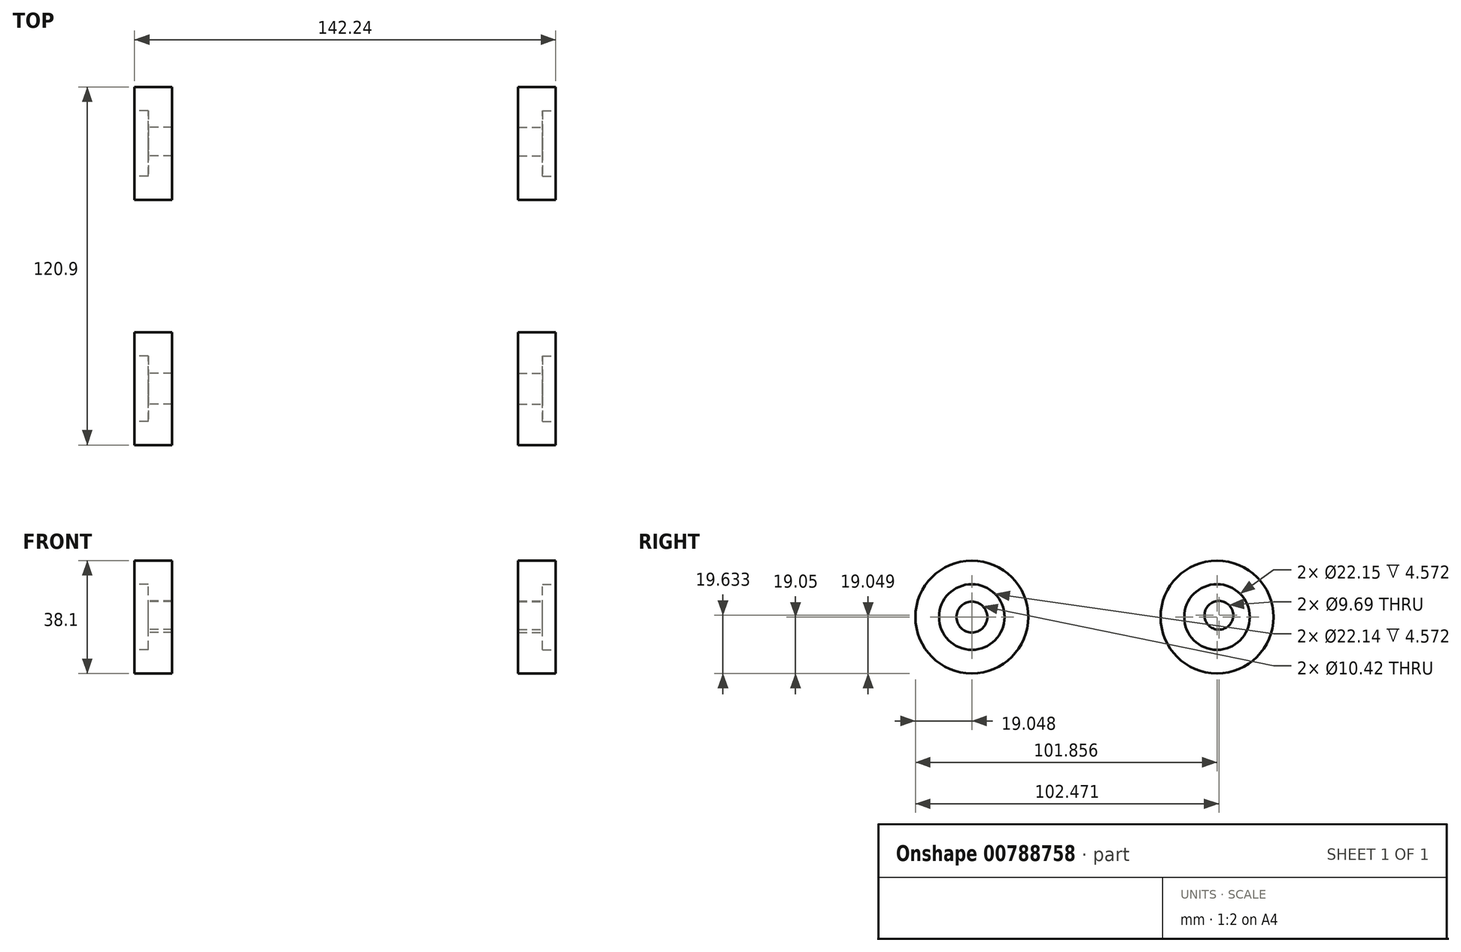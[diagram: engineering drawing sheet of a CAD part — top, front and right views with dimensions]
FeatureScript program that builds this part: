
annotation { "Feature Type Name" : "Feature", "Feature Type Description" : "" }
export const myFeature = defineFeature(function(context is Context, id is Id, definition is map)
    precondition{}
    {
        {
            var Q0;
            Q0=qCreatedBy(makeId("Right.planeOp"),FACE);
            var sketch = newSketch(context, id + "F0", { "sketchPlane" : qUnion([Q0])});
            skCircle(sketch, "E0", {"center": v(-41.4, -31.75) * mm, "radius": 19.05 * mm});
            skCircle(sketch, "E1", {"center": v(41.4, -31.75) * mm, "radius": 19.05 * mm});
            skSolve(sketch);
        }
        {
            var Q0;
            Q0=makeQuery(id+"F0.imprint","IMPRINT",FACE,{"disambiguationData":[TD([[makeQuery(id+"F0.imprint","IMPRINT",EDGE,{"derivedFrom":sQuery(id+"F0.wireOp",EDGE,"E0")}),1.0]])]});
            var Q1;
            Q1=makeQuery(id+"F0.imprint","IMPRINT",FACE,{"disambiguationData":[TD([[makeQuery(id+"F0.imprint","IMPRINT",EDGE,{"derivedFrom":sQuery(id+"F0.wireOp",EDGE,"E1")}),1.0]])]});
            extrude(context, id + "F1", {"entities" : qUnion([Q0, Q1]), "depth" : 71.12 * mm, "offsetDistance" : 25.4 * mm, "hasSecondDirection" : true, "secondDirectionOppositeDirection" : false, "secondDirectionDepth" : 58.42 * mm});
        }
        {
            var Q0;
            Q0=makeQuery(id+"F1.opExtrude","CAP_FACE",FACE,{"disambiguationData":[OSD([sQuery(id+"F0.wireOp",EDGE,"E0")])],"isStart":false});
            var sketch = newSketch(context, id + "F2", { "sketchPlane" : qUnion([Q0])});
            skCircle(sketch, "E2", {"center": v(-41.4, -31.75) * mm, "radius": 11.07 * mm});
            skCircle(sketch, "E3", {"center": v(41.4, -31.75) * mm, "radius": 11.07 * mm});
            skSolve(sketch);
        }
        {
            var Q0;
            Q0=makeQuery(id+"F2.imprint","IMPRINT",FACE,{"disambiguationData":[TD([[makeQuery(id+"F2.imprint","IMPRINT",EDGE,{"derivedFrom":sQuery(id+"F2.wireOp",EDGE,"E2")}),1.0]])]});
            var Q1;
            Q1=makeQuery(id+"F2.imprint","IMPRINT",FACE,{"disambiguationData":[TD([[makeQuery(id+"F2.imprint","IMPRINT",EDGE,{"derivedFrom":sQuery(id+"F2.wireOp",EDGE,"E3")}),1.0]])]});
            extrude(context, id + "F3", {"entities" : qUnion([Q0, Q1]), "operationType" : NewBodyOperationType.REMOVE, "oppositeDirection" : true, "depth" : 4.57 * mm, "offsetDistance" : 25.4 * mm});
        }
        {
            var Q0;
            Q0=makeQuery(id+"F3.boolean.opBoolean","COPY",FACE,{"derivedFrom":makeQuery(id+"F3.opExtrude","CAP_FACE",FACE,{"disambiguationData":[OSD([sQuery(id+"F2.wireOp",EDGE,"E2")])],"isStart":false})});
            var sketch = newSketch(context, id + "F4", { "sketchPlane" : qUnion([Q0])});
            skCircle(sketch, "E4", {"center": v(-41.4, -31.75) * mm, "radius": 5.21 * mm});
            skCircle(sketch, "E5", {"center": v(42.02, -31.17) * mm, "radius": 4.84 * mm});
            skSolve(sketch);
        }
        {
            var Q0;
            Q0=makeQuery(id+"F4.imprint","IMPRINT",FACE,{"disambiguationData":[TD([[makeQuery(id+"F4.imprint","IMPRINT",EDGE,{"derivedFrom":sQuery(id+"F4.wireOp",EDGE,"E4")}),1.0]])]});
            var Q1;
            Q1=makeQuery(id+"F4.imprint","IMPRINT",FACE,{"disambiguationData":[TD([[makeQuery(id+"F4.imprint","IMPRINT",EDGE,{"derivedFrom":sQuery(id+"F4.wireOp",EDGE,"E5")}),1.0]])]});
            extrude(context, id + "F5", {"entities" : qUnion([Q0, Q1]), "operationType" : NewBodyOperationType.REMOVE, "oppositeDirection" : true, "depth" : 40.64 * mm, "offsetDistance" : 25.4 * mm});
        }
        {
            var Q0;
            Q0=makeQuery(id+"F1.opExtrude","SWEPT_BODY",BODY,{"disambiguationData":[OSD([sQuery(id+"F0.wireOp",EDGE,"E0")])]});
            var Q1;
            Q1=makeQuery(id+"F1.opExtrude","SWEPT_BODY",BODY,{"disambiguationData":[OSD([sQuery(id+"F0.wireOp",EDGE,"E1")])]});
            var Q2;
            Q2=qCreatedBy(makeId("Right.planeOp"),FACE);
            mirror(context, id + "F6", {"entities" : qUnion([Q0, Q1]), "mirrorPlane" : qUnion([Q2])});
        }
    });
